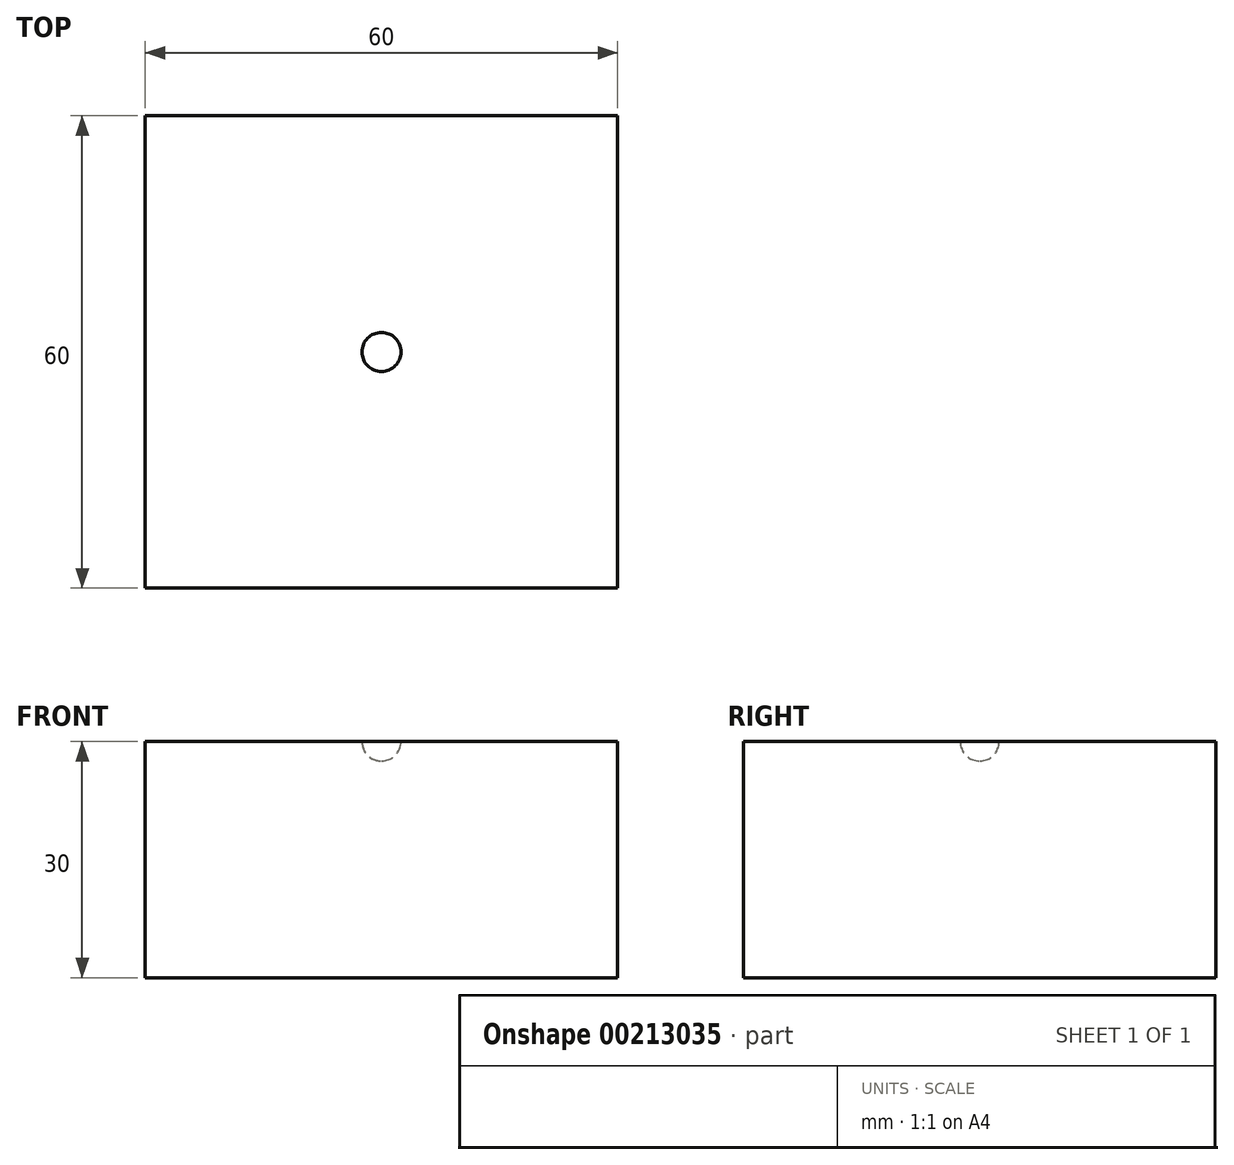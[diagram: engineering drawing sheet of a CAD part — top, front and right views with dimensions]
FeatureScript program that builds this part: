
annotation { "Feature Type Name" : "Feature", "Feature Type Description" : "" }
export const myFeature = defineFeature(function(context is Context, id is Id, definition is map)
    precondition{}
    {
        {
            var Q0;
            Q0=qCreatedBy(makeId("Top.planeOp"),FACE);
            var sketch = newSketch(context, id + "F0", { "sketchPlane" : qUnion([Q0])});
            skPoint(sketch, "E0.middle", {"position": v(0, 0) * mm});
            skLineSegment(sketch, "E1.bottom", {"start": v(30, -30) * mm, "end": v(-30, -30) * mm});
            skLineSegment(sketch, "E1.top", {"start": v(30, 30) * mm, "end": v(-30, 30) * mm});
            skLineSegment(sketch, "E1.left", {"start": v(30, -30) * mm, "end": v(30, 30) * mm});
            skLineSegment(sketch, "E1.right", {"start": v(-30, -30) * mm, "end": v(-30, 30) * mm});
            skSolve(sketch);
        }
        {
            var Q0;
            Q0 = qSketchRegion(id + "F0", true);
            extrude(context, id + "F1", {"entities" : qUnion([Q0]), "depth" : 30 * mm});
        }
        {
            var Q0;
            Q0=qCreatedBy(makeId("Front.planeOp"),FACE);
            var sketch = newSketch(context, id + "F2", { "sketchPlane" : qUnion([Q0])});
            skArc(sketch, "E2", {"start": v(0, 32.47) * mm, "mid": v(-2.48, 30) * mm, "end": v(0, 27.52) * mm});
            skLineSegment(sketch, "E3", {"start": v(0, 32.47) * mm, "end": v(0, 27.52) * mm});
            skSolve(sketch);
        }
        {
            var Q0;
            Q0 = qSketchRegion(id + "F2", true);
            var Q1;
            Q1=sQuery(id+"F2.wireOp",EDGE,"E3");
            revolve(context, id + "F3", {"operationType" : NewBodyOperationType.REMOVE, "entities" : qUnion([Q0]), "axis" : qUnion([Q1]), "revolveType" : RevolveType.FULL, "oppositeDirection" : true});
        }
    });
